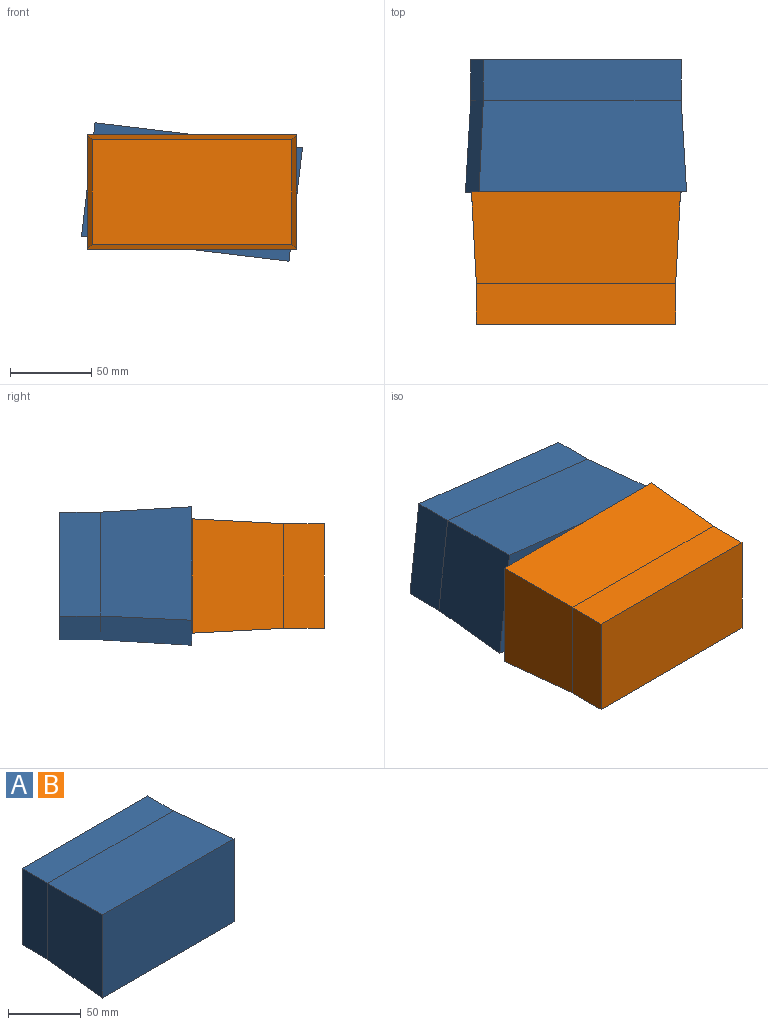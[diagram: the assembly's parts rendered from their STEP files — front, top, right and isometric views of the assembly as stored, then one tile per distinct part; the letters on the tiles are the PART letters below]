
ASSEMBLY  parts=2 mates=1
PART A: 10 faces, bbox 128.2x81.2x70.1 mm
  f0: plane 70.09x56.18mm, normal (1,0.05,0), area 3777.5mm2, adj f1,f3,f4,f9
  f1: plane 128.21x56.18mm, normal (0,0.05,1), area 7046.9mm2, adj f0,f2,f4,f8
  f2: plane 70.09x56.18mm, normal (-1,0.05,0), area 3777.5mm2, adj f1,f3,f4,f7
  f3: plane 128.21x56.18mm, normal (0,0.05,-1), area 7046.9mm2, adj f0,f2,f4,f6
  f4: plane 128.21x70.09mm, normal (0,-1,0), area 8986.6mm2, adj f0,f1,f2,f3
  f5: plane 122.32x64.2mm, normal (0,1,0), area 7853.6mm2, adj f6,f7,f8,f9
  f6: plane 122.32x25mm, normal (0,0,-1), area 3058.1mm2, adj f3,f5,f7,f9
  f7: plane 64.2x25mm, normal (-1,0,0), area 1605.1mm2, adj f2,f5,f6,f8
  f8: plane 122.32x25mm, normal (0,0,1), area 3058.1mm2, adj f1,f5,f7,f9
  f9: plane 64.2x25mm, normal (1,0,0), area 1605.1mm2, adj f0,f5,f6,f8
PART B: same geometry as A
PLACE A rot(axis=(0,-1,0),173.1deg) t=(123.33,-95.33,59.69)mm
PLACE B rot(axis=(1,0,0),180deg) t=(-2.39,-207.69,67.23)mm fixed
MATE revolute B.f4 <-> A.f4  axis (0,1,0) through (58.77,-151.51,35.13)mm
